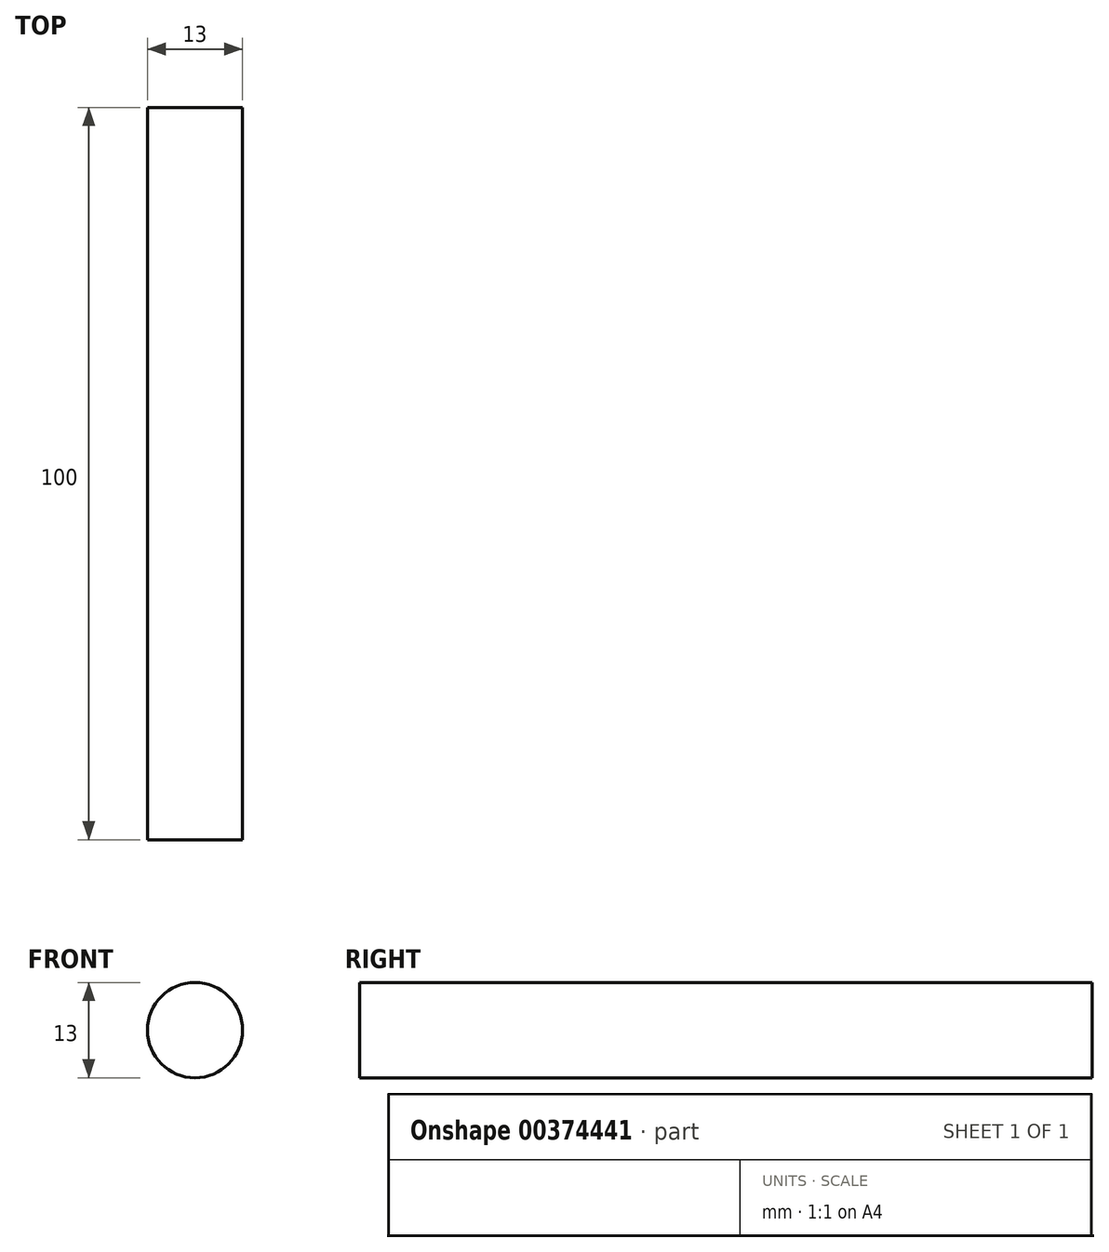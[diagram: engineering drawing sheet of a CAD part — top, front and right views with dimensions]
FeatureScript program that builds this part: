
annotation { "Feature Type Name" : "Feature", "Feature Type Description" : "" }
export const myFeature = defineFeature(function(context is Context, id is Id, definition is map)
    precondition{}
    {
        {
            var Q0;
            Q0=qCreatedBy(makeId("Front.planeOp"),FACE);
            var sketch = newSketch(context, id + "F0", { "sketchPlane" : qUnion([Q0])});
            skCircle(sketch, "E0", {"center": v(0, 0) * mm, "radius": 6.5 * mm});
            skSolve(sketch);
        }
        {
            var Q0;
            Q0=makeQuery(id+"F0.imprint","IMPRINT",FACE,{"disambiguationData":[TD([[makeQuery(id+"F0.imprint","IMPRINT",EDGE,{"derivedFrom":sQuery(id+"F0.wireOp",EDGE,"E0")}),1.0]])]});
            extrude(context, id + "F1", {"entities" : qUnion([Q0]), "depth" : 100 * mm});
        }
    });
